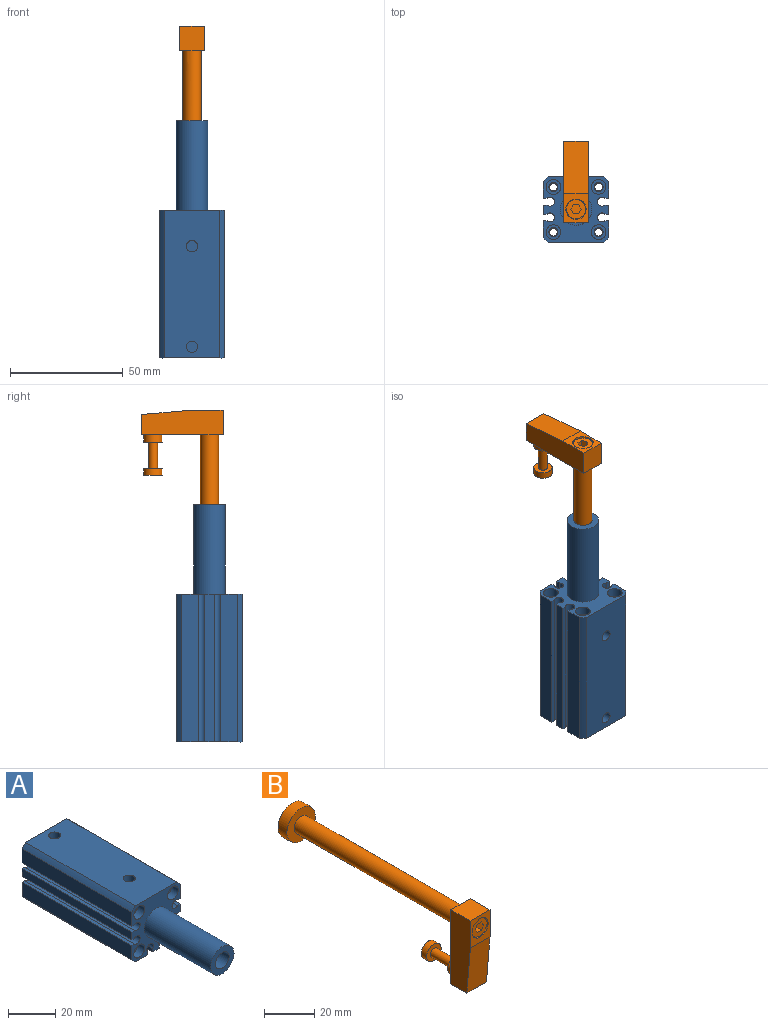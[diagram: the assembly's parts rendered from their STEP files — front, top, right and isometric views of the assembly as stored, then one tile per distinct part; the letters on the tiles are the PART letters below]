
ASSEMBLY  parts=2 mates=1
PART A: 86 faces, bbox 29x105x29 mm
  f0: cylinder r=4.05mm len=51mm, axis (0,-1,0), area 1297.8mm2, adj f82,f85
  f1: cylinder r=8mm len=42.5mm, axis (0,1,0), area 2136.3mm2, adj f84,f85
  f2: cylinder r=4.05mm len=8.1mm, axis (0,-1,0), area 165.4mm2, adj f83,f84
  f3: cylinder r=7mm len=39.5mm, axis (0,1,0), area 1737.3mm2, adj f32,f82
  f4: cylinder r=2.5mm len=5mm, axis (0,0,1), area 78.5mm2, adj f52,f81
  f5: cylinder r=2.5mm len=5mm, axis (0,0,1), area 78.5mm2, adj f52,f80
  f6: cylinder r=2mm len=7mm, axis (0,1,0), area 88mm2, adj f33,f79
  f7: cylinder r=2mm len=7mm, axis (0,1,0), area 88mm2, adj f34,f78
  f8: cylinder r=2mm len=7mm, axis (0,1,0), area 88mm2, adj f35,f77
  f9: cylinder r=2mm len=7mm, axis (0,1,0), area 88mm2, adj f36,f76
  f10: cylinder r=3.25mm len=6.5mm, axis (0,1,0), area 81.7mm2, adj f33,f37
  f11: cylinder r=3.25mm len=6.5mm, axis (0,1,0), area 81.7mm2, adj f34,f37
  f12: cylinder r=3.25mm len=6.5mm, axis (0,1,0), area 81.7mm2, adj f35,f37
  f13: cylinder r=3.25mm len=6.5mm, axis (0,1,0), area 81.7mm2, adj f36,f37
  f14: cylinder r=2mm len=7mm, axis (0,-1,0), area 88mm2, adj f71,f75
  f15: cylinder r=2mm len=7mm, axis (0,-1,0), area 88mm2, adj f70,f74
  f16: cylinder r=2mm len=7mm, axis (0,-1,0), area 88mm2, adj f69,f73
  f17: cylinder r=2mm len=7mm, axis (0,-1,0), area 88mm2, adj f68,f72
  f18: cylinder r=3.25mm len=6.5mm, axis (0,-1,0), area 81.7mm2, adj f32,f71
  f19: cylinder r=3.25mm len=6.5mm, axis (0,-1,0), area 81.7mm2, adj f32,f70
  f20: cylinder r=3.25mm len=6.5mm, axis (0,-1,0), area 81.7mm2, adj f32,f69
  f21: cylinder r=3.25mm len=6.5mm, axis (0,-1,0), area 81.7mm2, adj f32,f68
  f22: cylinder r=2mm len=65.5mm, axis (0,-1,0), area 600.9mm2, adj f32,f37,f60,f61
  f23: cylinder r=2mm len=65.5mm, axis (0,-1,0), area 600.9mm2, adj f32,f37,f58,f59
  f24: cylinder r=2mm len=65.5mm, axis (0,-1,0), area 600.9mm2, adj f32,f37,f56,f57
  f25: cylinder r=2mm len=65.5mm, axis (0,-1,0), area 600.9mm2, adj f32,f37,f54,f55
  f26: cylinder r=4.25mm len=8.5mm, axis (0,-1,0), area 53.4mm2, adj f44,f53
  f27: cylinder r=8.5mm len=17mm, axis (0,1,0), area 160.2mm2, adj f37,f44
  f28: cylinder r=1.75mm len=43.5mm, axis (0,1,0), area 478.3mm2, adj f72,f76
  f29: cylinder r=1.75mm len=43.5mm, axis (0,1,0), area 478.3mm2, adj f73,f77
  f30: cylinder r=1.75mm len=43.5mm, axis (0,1,0), area 478.3mm2, adj f74,f78
  f31: cylinder r=1.75mm len=43.5mm, axis (0,1,0), area 478.3mm2, adj f75,f79
  f32: plane 29x29mm, normal (0,-1,0), area 447.9mm2, adj f3,f18,f19,f20,f21,f22,f23,f24
  f33: plane 6.5x6.5mm, normal (0,1,0), area 20.6mm2, adj f6,f10
  f34: plane 6.5x6.5mm, normal (0,1,0), area 20.6mm2, adj f7,f11
  f35: plane 6.5x6.5mm, normal (0,1,0), area 20.6mm2, adj f8,f12
  f36: plane 6.5x6.5mm, normal (0,1,0), area 20.6mm2, adj f9,f13
  f37: plane 29x29mm, normal (0,1,0), area 374.8mm2, adj f10,f11,f12,f13,f22,f23,f24,f25
  f38: plane 65.5x7.28mm, normal (1,0,0), area 476.7mm2, adj f32,f37,f51,f66
  f39: plane 65.5x7.28mm, normal (1,0,0), area 476.7mm2, adj f32,f37,f49,f62
  f40: plane 65.5x7.28mm, normal (0,0,-1), area 476.7mm2, adj f32,f37,f49,f60
  f41: plane 65.5x7.28mm, normal (0,0,-1), area 476.7mm2, adj f32,f37,f47,f58
  f42: plane 65.5x7.28mm, normal (-1,0,0), area 476.7mm2, adj f32,f37,f47,f56
  f43: plane 65.5x7.28mm, normal (-1,0,0), area 476.7mm2, adj f32,f37,f45,f54
  f44: plane 17x17mm, normal (0,1,0), area 170.2mm2, adj f26,f27
  f45: cylinder r=19mm len=65.5mm, axis (0,1,0), area 206.1mm2, adj f32,f37,f43,f52
  f46: plane 65.5x4mm, normal (-1,0,0), area 262mm2, adj f32,f37,f55,f57
  f47: cylinder r=19mm len=65.5mm, axis (0,1,0), area 206.1mm2, adj f32,f37,f41,f42
  f48: plane 65.5x4mm, normal (0,0,-1), area 262mm2, adj f32,f37,f59,f61
  f49: cylinder r=19mm len=65.5mm, axis (0,1,0), area 206.1mm2, adj f32,f37,f39,f40
  f50: plane 65.5x4mm, normal (1,0,0), area 262mm2, adj f32,f37,f64,f67
  f51: cylinder r=19mm len=65.5mm, axis (0,1,0), area 206.1mm2, adj f32,f37,f38,f52
  f52: plane 65.5x24.56mm, normal (0,0,1), area 1569.2mm2, adj f4,f5,f32,f37,f45,f51
  f53: plane 8.5x8.5mm, normal (0,1,0), area 56.7mm2, adj f26
  f54: plane 65.5x1.68mm, normal (0,0,-1), area 109.9mm2, adj f25,f32,f37,f43
  f55: plane 65.5x1.68mm, normal (0,0,1), area 109.9mm2, adj f25,f32,f37,f46
  f56: plane 65.5x1.68mm, normal (0,0,1), area 109.9mm2, adj f24,f32,f37,f42
  f57: plane 65.5x1.68mm, normal (0,0,-1), area 109.9mm2, adj f24,f32,f37,f46
  f58: plane 65.5x1.68mm, normal (1,0,0), area 109.9mm2, adj f23,f32,f37,f41
  f59: plane 65.5x1.68mm, normal (-1,0,0), area 109.9mm2, adj f23,f32,f37,f48
  f60: plane 65.5x1.68mm, normal (-1,0,0), area 109.9mm2, adj f22,f32,f37,f40
  f61: plane 65.5x1.68mm, normal (1,0,0), area 109.9mm2, adj f22,f32,f37,f48
  f62: plane 65.5x1.68mm, normal (0,0,1), area 109.9mm2, adj f32,f37,f39,f63
  f63: cylinder r=2mm len=65.5mm, axis (0,-1,0), area 600.9mm2, adj f32,f37,f62,f64
  f64: plane 65.5x1.68mm, normal (0,0,-1), area 109.9mm2, adj f32,f37,f50,f63
  f65: cylinder r=2mm len=65.5mm, axis (0,-1,0), area 600.9mm2, adj f32,f37,f66,f67
  f66: plane 65.5x1.68mm, normal (0,0,-1), area 109.9mm2, adj f32,f37,f38,f65
  f67: plane 65.5x1.68mm, normal (0,0,1), area 109.9mm2, adj f32,f37,f50,f65
  f68: plane 6.5x6.5mm, normal (0,-1,0), area 20.6mm2, adj f17,f21
  f69: plane 6.5x6.5mm, normal (0,-1,0), area 20.6mm2, adj f16,f20
  f70: plane 6.5x6.5mm, normal (0,-1,0), area 20.6mm2, adj f15,f19
  f71: plane 6.5x6.5mm, normal (0,-1,0), area 20.6mm2, adj f14,f18
  f72: plane 4x4mm, normal (0,-1,0), area 2.9mm2, adj f17,f28
  f73: plane 4x4mm, normal (0,-1,0), area 2.9mm2, adj f16,f29
  f74: plane 4x4mm, normal (0,-1,0), area 2.9mm2, adj f15,f30
  f75: plane 4x4mm, normal (0,-1,0), area 2.9mm2, adj f14,f31
  f76: plane 4x4mm, normal (0,1,0), area 2.9mm2, adj f9,f28
  f77: plane 4x4mm, normal (0,1,0), area 2.9mm2, adj f8,f29
  f78: plane 4x4mm, normal (0,1,0), area 2.9mm2, adj f7,f30
  f79: plane 4x4mm, normal (0,1,0), area 2.9mm2, adj f6,f31
  f80: plane 5x5mm, normal (0,0,1), area 19.6mm2, adj f5
  f81: plane 5x5mm, normal (0,0,1), area 19.6mm2, adj f4
  f82: plane 14x14mm, normal (0,-1,0), area 102.4mm2, adj f0,f3
  f83: plane 8.1x8.1mm, normal (0,-1,0), area 51.5mm2, adj f2
  f84: plane 16x16mm, normal (0,-1,0), area 149.5mm2, adj f1,f2
  f85: plane 16x16mm, normal (0,1,0), area 149.5mm2, adj f0,f1
PART B: 28 faces, bbox 16x105.5x38 mm
  f0: cylinder r=4.05mm len=8.1mm, axis (0,-1,0), area 81.4mm2, adj f7,f27
  f1: cylinder r=2mm len=11.8mm, axis (0,-1,0), area 148.3mm2, adj f26,f27
  f2: cylinder r=4.05mm len=8.1mm, axis (0,-1,0), area 76.3mm2, adj f25,f26
  f3: cylinder r=4.25mm len=8.5mm, axis (0,1,0), area 133.5mm2, adj f8,f17
  f4: cylinder r=4.5mm len=9mm, axis (0,-1,0), area 155.5mm2, adj f8,f16
  f5: cylinder r=8mm len=16mm, axis (0,1,0), area 251.3mm2, adj f9,f10
  f6: cylinder r=4mm len=89.5mm, axis (0,1,0), area 2249.4mm2, adj f7,f9
  f7: plane 36x11mm, normal (0,1,0), area 294.2mm2, adj f0,f6,f11,f12,f14,f15
  f8: plane 9x9mm, normal (0,-1,0), area 6.9mm2, adj f3,f4
  f9: plane 16x16mm, normal (0,-1,0), area 150.8mm2, adj f5,f6
  f10: plane 16x16mm, normal (0,1,0), area 201.1mm2, adj f5
  f11: plane 11x11mm, normal (0,0,1), area 121mm2, adj f7,f14,f15,f16
  f12: plane 11x9mm, normal (0,0,-1), area 99mm2, adj f7,f13,f14,f15
  f13: plane 22.86x11mm, normal (0,-1,-0.09), area 252.4mm2, adj f12,f14,f15,f16
  f14: plane 36x11mm, normal (-1,0,0), area 373.1mm2, adj f7,f11,f12,f13,f16
  f15: plane 36x11mm, normal (1,0,0), area 373.1mm2, adj f7,f11,f12,f13,f16
  f16: plane 13.14x11mm, normal (0,-1,0), area 80.9mm2, adj f4,f11,f13,f14,f15
  f17: plane 8.5x8.5mm, normal (0,-1,0), area 42.9mm2, adj f3,f18,f19,f20,f21,f22,f23
  f18: plane 5x2mm, normal (-0.87,0,0.5), area 11.5mm2, adj f17,f19,f23,f24
  f19: plane 5x2mm, normal (-0.87,0,-0.5), area 11.5mm2, adj f17,f18,f20,f24
  f20: plane 5x2.31mm, normal (0,0,-1), area 11.5mm2, adj f17,f19,f21,f24
  f21: plane 5x2mm, normal (0.87,0,-0.5), area 11.5mm2, adj f17,f20,f22,f24
  f22: plane 5x2mm, normal (0.87,0,0.5), area 11.5mm2, adj f17,f21,f23,f24
  f23: plane 5x2.31mm, normal (0,0,1), area 11.5mm2, adj f17,f18,f22,f24
  f24: plane 4.62x4mm, normal (0,-1,0), area 13.9mm2, adj f18,f19,f20,f21,f22,f23
  f25: plane 8.1x8.1mm, normal (0,1,0), area 51.5mm2, adj f2
  f26: plane 8.1x8.1mm, normal (0,-1,0), area 39mm2, adj f1,f2
  f27: plane 8.1x8.1mm, normal (0,1,0), area 39mm2, adj f0,f1
PLACE A rot(axis=(0,-0.71,0.71),180deg) t=(0,0,-30)mm
PLACE B rot(axis=(0,-0.71,0.71),180deg) t=(0,0,-18.75)mm
MATE fastened A.f1 <-> B.f3  axis (0,0,1) through (0,0,-51.25)mm
